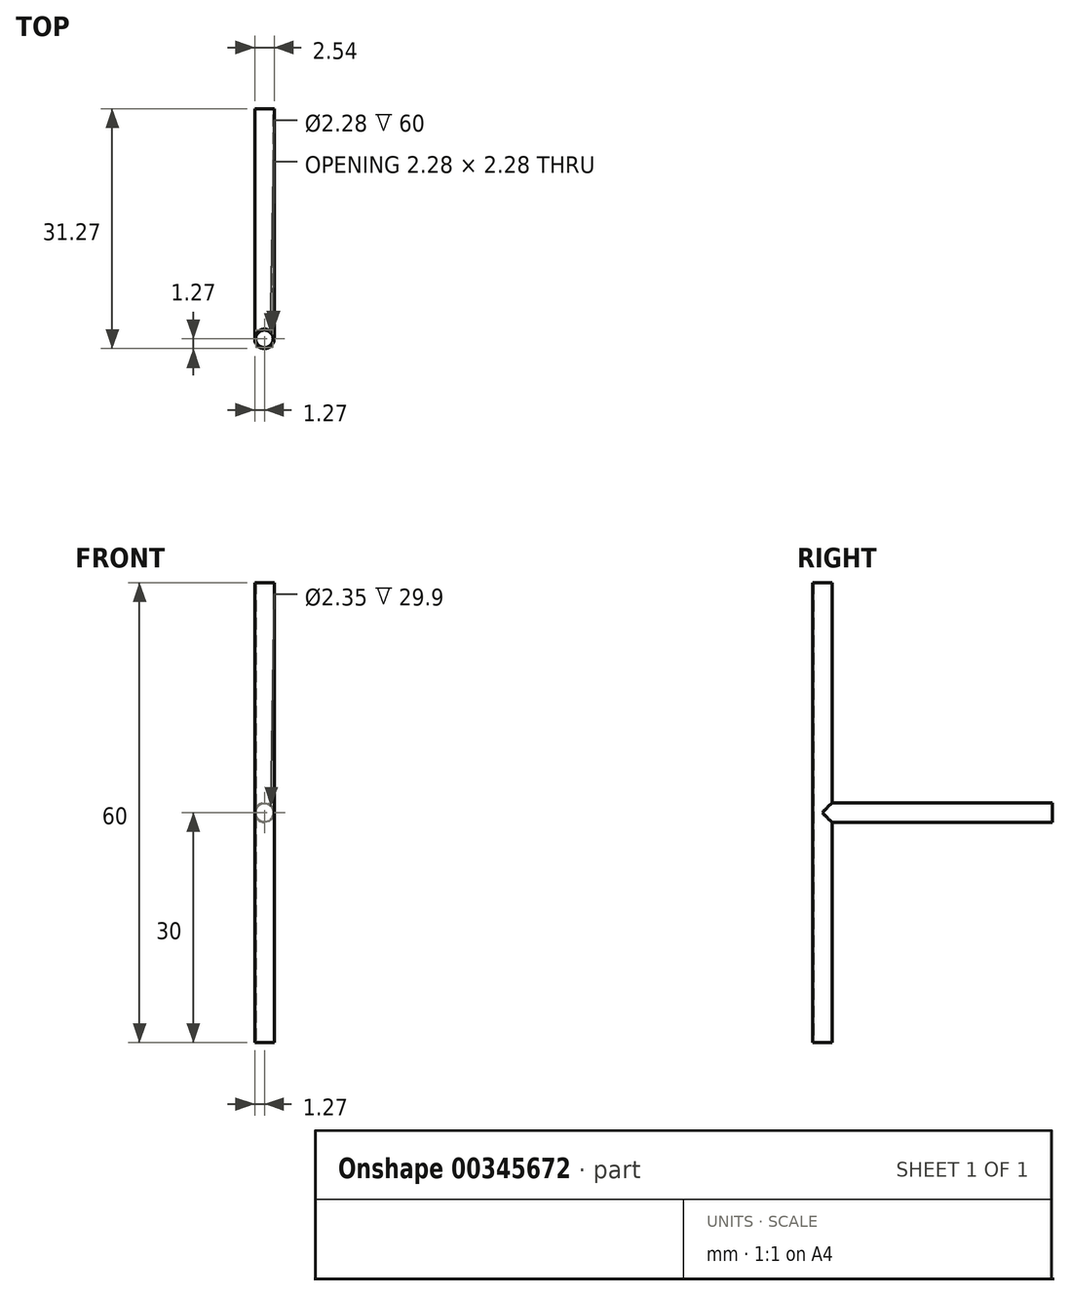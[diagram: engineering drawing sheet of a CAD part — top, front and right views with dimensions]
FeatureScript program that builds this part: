
annotation { "Feature Type Name" : "Feature", "Feature Type Description" : "" }
export const myFeature = defineFeature(function(context is Context, id is Id, definition is map)
    precondition{}
    {
        {
            var Q0;
            Q0=qCreatedBy(makeId("Top.planeOp"),FACE);
            var sketch = newSketch(context, id + "F0", { "sketchPlane" : qUnion([Q0])});
            skCircle(sketch, "E0", {"center": v(0, 0) * mm, "radius": 1.27 * mm});
            skSolve(sketch);
        }
        {
            var Q0;
            Q0=makeQuery(id+"F0.imprint","IMPRINT",FACE,{"disambiguationData":[TD([[makeQuery(id+"F0.imprint","IMPRINT",EDGE,{"derivedFrom":sQuery(id+"F0.wireOp",EDGE,"E0")}),1.0]])]});
            extrude(context, id + "F1", {"entities" : qUnion([Q0]), "oppositeDirection" : true, "depth" : 30 * mm, "hasSecondDirection" : true, "secondDirectionOppositeDirection" : false, "secondDirectionDepth" : 30 * mm});
        }
        {
            var Q0;
            Q0=makeQuery(id+"F1.opExtrude","CAP_FACE",FACE,{"disambiguationData":[OSD([sQuery(id+"F0.wireOp",EDGE,"E0")])],"isStart":false});
            var sketch = newSketch(context, id + "F2", { "sketchPlane" : qUnion([Q0])});
            skCircle(sketch, "E1", {"center": v(0, 0) * mm, "radius": 1.14 * mm});
            skSolve(sketch);
        }
        {
            var Q0;
            Q0=makeQuery(id+"F2.imprint","IMPRINT",FACE,{"disambiguationData":[TD([[makeQuery(id+"F2.imprint","IMPRINT",EDGE,{"derivedFrom":sQuery(id+"F2.wireOp",EDGE,"E1")}),1.0]])]});
            extrude(context, id + "F3", {"entities" : qUnion([Q0]), "operationType" : NewBodyOperationType.REMOVE, "oppositeDirection" : true, "depth" : 100 * mm});
        }
        {
            var Q0;
            Q0=qCreatedBy(makeId("Front.planeOp"),FACE);
            var sketch = newSketch(context, id + "F4", { "sketchPlane" : qUnion([Q0])});
            skCircle(sketch, "E2", {"center": v(0, 0) * mm, "radius": 1.27 * mm});
            skSolve(sketch);
        }
        {
            var Q0;
            Q0=qSketchRegion(id+"F4",true);
            extrude(context, id + "F5", {"entities" : qUnion([Q0]), "operationType" : NewBodyOperationType.ADD, "oppositeDirection" : true, "depth" : 30 * mm});
        }
        {
            var Q0;
            Q0=makeQuery(id+"F5.opExtrude","CAP_FACE",FACE,{"disambiguationData":[OSD([sQuery(id+"F4.wireOp",EDGE,"E2")])],"isStart":false});
            var sketch = newSketch(context, id + "F6", { "sketchPlane" : qUnion([Q0])});
            skCircle(sketch, "E3", {"center": v(0, 0) * mm, "radius": 1.17 * mm});
            skSolve(sketch);
        }
        {
            var Q0;
            Q0=qSketchRegion(id+"F6",true);
            extrude(context, id + "F7", {"entities" : qUnion([Q0]), "operationType" : NewBodyOperationType.REMOVE, "oppositeDirection" : true, "depth" : 29.9 * mm});
        }
        {
            var Q0;
            Q0=makeQuery(id+"F1.opExtrude","CAP_FACE",FACE,{"disambiguationData":[OSD([sQuery(id+"F0.wireOp",EDGE,"E0")])],"isStart":false});
            var sketch = newSketch(context, id + "F8", { "sketchPlane" : qUnion([Q0])});
            skCircle(sketch, "E4", {"center": v(0, 0) * mm, "radius": 1.14 * mm});
            skSolve(sketch);
        }
        {
            var Q0;
            Q0=qSketchRegion(id+"F8",true);
            extrude(context, id + "F9", {"entities" : qUnion([Q0]), "operationType" : NewBodyOperationType.REMOVE, "oppositeDirection" : true, "depth" : 68.19 * mm});
        }
    });
